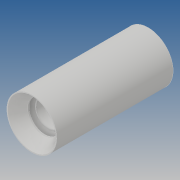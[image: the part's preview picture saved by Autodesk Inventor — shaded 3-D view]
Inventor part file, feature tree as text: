
AUTODESK INVENTOR PART (.ipt)
format: ipt  version: 2019 (Build 230136000, 136)  size: 143,872 bytes
history: native  units: mm
features: other x3, sketch x3, chamfer x2, extrude x1, projected_geometry x1
ambient origin geometry x8: Origin, YZ Plane, XZ Plane, XY Plane, X Axis, Y Axis, Z Axis, Center Point
bodies: Solide1 (feature_tree)
feature tree (10):
  other  "Révolution1"
  chamfer  "Chanfrein1"  Distance=19.0mm
  chamfer  "Chanfrein2"  Distance=10.0mm
  other  "Plan de construction1"
  extrude  "Extrusion1"  Depth=2.0mm
  other  "Révolution2"
  sketch  "Esquisse1"
  sketch  "Esquisse3"
  sketch  "Esquisse4"
  projected_geometry  "Boucle projetée1"
